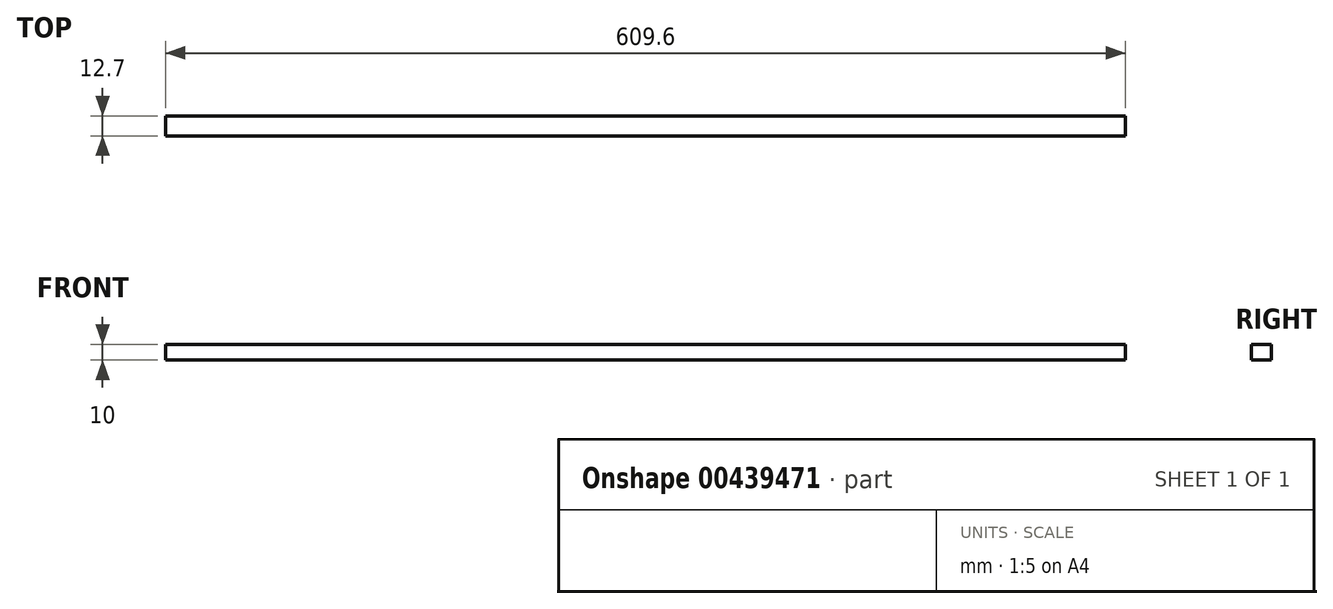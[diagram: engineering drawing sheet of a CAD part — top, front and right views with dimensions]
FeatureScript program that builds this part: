
annotation { "Feature Type Name" : "Feature", "Feature Type Description" : "" }
export const myFeature = defineFeature(function(context is Context, id is Id, definition is map)
    precondition{}
    {
        {
            var Q0;
            Q0=qCreatedBy(makeId("Front.planeOp"),FACE);
            var sketch = newSketch(context, id + "F0", { "sketchPlane" : qUnion([Q0])});
            skLineSegment(sketch, "E0.bottom", {"start": v(304.8, 5) * mm, "end": v(-304.8, 5) * mm});
            skLineSegment(sketch, "E0.top", {"start": v(304.8, -5) * mm, "end": v(-304.8, -5) * mm});
            skLineSegment(sketch, "E0.left", {"start": v(304.8, 5) * mm, "end": v(304.8, -5) * mm});
            skLineSegment(sketch, "E0.right", {"start": v(-304.8, 5) * mm, "end": v(-304.8, -5) * mm});
            skPoint(sketch, "E0.middle", {"position": v(0, 0) * mm});
            skSolve(sketch);
        }
        {
            var Q0;
            Q0 = qSketchRegion(id + "F0", true);
            extrude(context, id + "F1", {"entities" : qUnion([Q0]), "depth" : 12.7 * mm});
        }
    });
